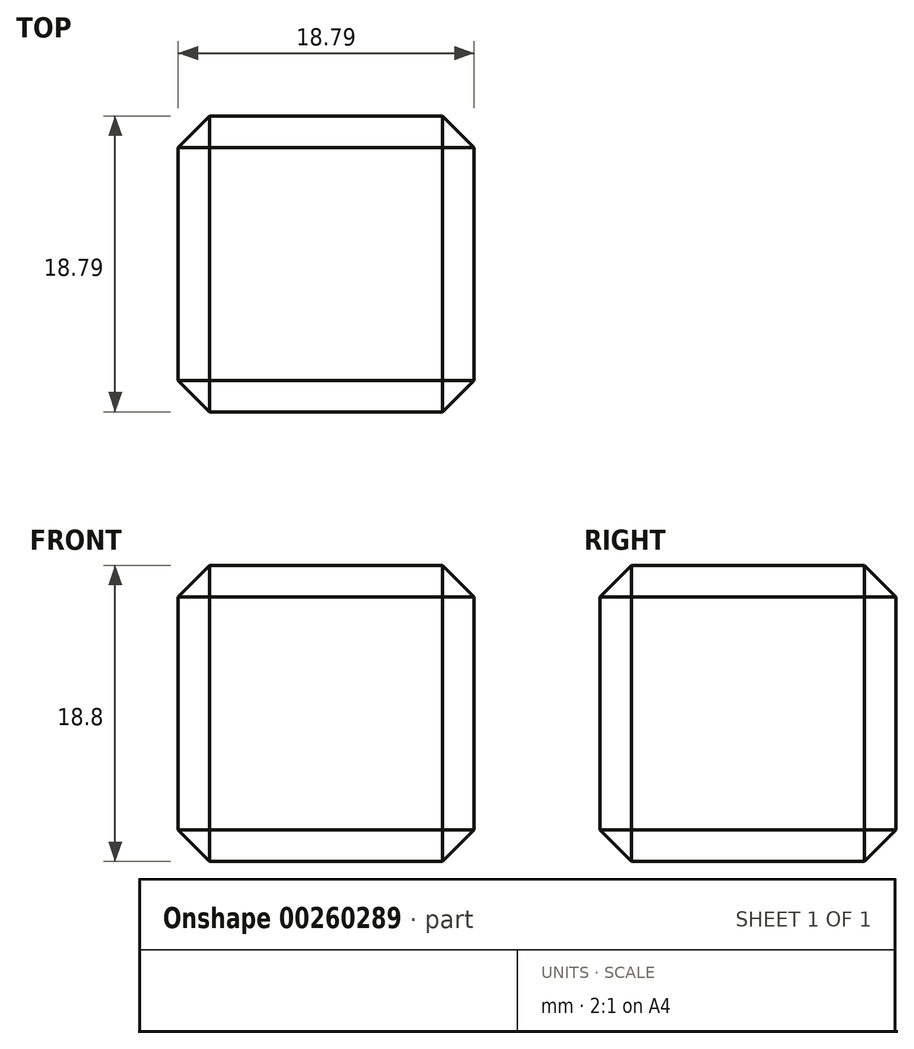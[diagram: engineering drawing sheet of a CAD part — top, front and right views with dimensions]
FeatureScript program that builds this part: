
annotation { "Feature Type Name" : "Feature", "Feature Type Description" : "" }
export const myFeature = defineFeature(function(context is Context, id is Id, definition is map)
    precondition{}
    {
        {
            var Q0;
            Q0=qCreatedBy(makeId("Top.planeOp"),FACE);
            var sketch = newSketch(context, id + "F0", { "sketchPlane" : qUnion([Q0])});
            skLineSegment(sketch, "E0.bottom", {"start": v(-42.6, -27.1) * mm, "end": v(-23.8, -27.1) * mm});
            skLineSegment(sketch, "E0.top", {"start": v(-42.6, -8.3) * mm, "end": v(-23.8, -8.3) * mm});
            skLineSegment(sketch, "E0.left", {"start": v(-42.6, -27.1) * mm, "end": v(-42.6, -8.3) * mm});
            skLineSegment(sketch, "E0.right", {"start": v(-23.8, -27.1) * mm, "end": v(-23.8, -8.3) * mm});
            skSolve(sketch);
        }
        {
            var Q0;
            Q0=makeQuery(id+"F0.imprint","IMPRINT",FACE,{"disambiguationData":[TD([[makeQuery(id+"F0.imprint","IMPRINT",EDGE,{"derivedFrom":sQuery(id+"F0.wireOp",EDGE,"E0.bottom")}),1.0]])]});
            extrude(context, id + "F1", {"entities" : qUnion([Q0]), "depth" : 18.8 * mm});
        }
        {
            var Q0;
            Q0=makeQuery(id+"F1.opExtrude","CAP_EDGE",EDGE,{"disambiguationData":[OSD([sQuery(id+"F0.wireOp",EDGE,"E0.left")])],"isStart":false});
            var Q1;
            Q1=makeQuery(id+"F1.opExtrude","CAP_EDGE",EDGE,{"disambiguationData":[OSD([sQuery(id+"F0.wireOp",EDGE,"E0.bottom")])],"isStart":false});
            var Q2;
            Q2=makeQuery(id+"F1.opExtrude","SWEPT_EDGE",EDGE,{"disambiguationData":[OSD([sQuery(id+"F0.wireOp",EDGE,"E0.bottom"),sQuery(id+"F0.wireOp",EDGE,"E0.left")])]});
            var Q3;
            Q3=makeQuery(id+"F1.opExtrude","SWEPT_EDGE",EDGE,{"disambiguationData":[OSD([sQuery(id+"F0.wireOp",EDGE,"E0.top"),sQuery(id+"F0.wireOp",EDGE,"E0.left")])]});
            var Q4;
            Q4=makeQuery(id+"F1.opExtrude","CAP_EDGE",EDGE,{"disambiguationData":[OSD([sQuery(id+"F0.wireOp",EDGE,"E0.left")])],"isStart":true});
            var Q5;
            Q5=makeQuery(id+"F1.opExtrude","CAP_EDGE",EDGE,{"disambiguationData":[OSD([sQuery(id+"F0.wireOp",EDGE,"E0.bottom")])],"isStart":true});
            var Q6;
            Q6=makeQuery(id+"F1.opExtrude","SWEPT_EDGE",EDGE,{"disambiguationData":[OSD([sQuery(id+"F0.wireOp",EDGE,"E0.bottom"),sQuery(id+"F0.wireOp",EDGE,"E0.right")])]});
            var Q7;
            Q7=makeQuery(id+"F1.opExtrude","CAP_EDGE",EDGE,{"disambiguationData":[OSD([sQuery(id+"F0.wireOp",EDGE,"E0.top")])],"isStart":false});
            var Q8;
            Q8=makeQuery(id+"F1.opExtrude","SWEPT_FACE",FACE,{"disambiguationData":[OSD([sQuery(id+"F0.wireOp",EDGE,"E0.right")])]});
            var Q9;
            Q9=makeQuery(id+"F1.opExtrude","CAP_EDGE",EDGE,{"disambiguationData":[OSD([sQuery(id+"F0.wireOp",EDGE,"E0.top")])],"isStart":true});
            chamfer(context, id + "F2", {"entities" : qUnion([Q0, Q1, Q2, Q3, Q4, Q5, Q6, Q7, Q8, Q9]), "chamferType" : ChamferType.OFFSET_ANGLE, "width" : 2 * mm, "oppositeDirection" : false, "angle" : 45 * degree, "tangentPropagation" : true});
        }
    });
